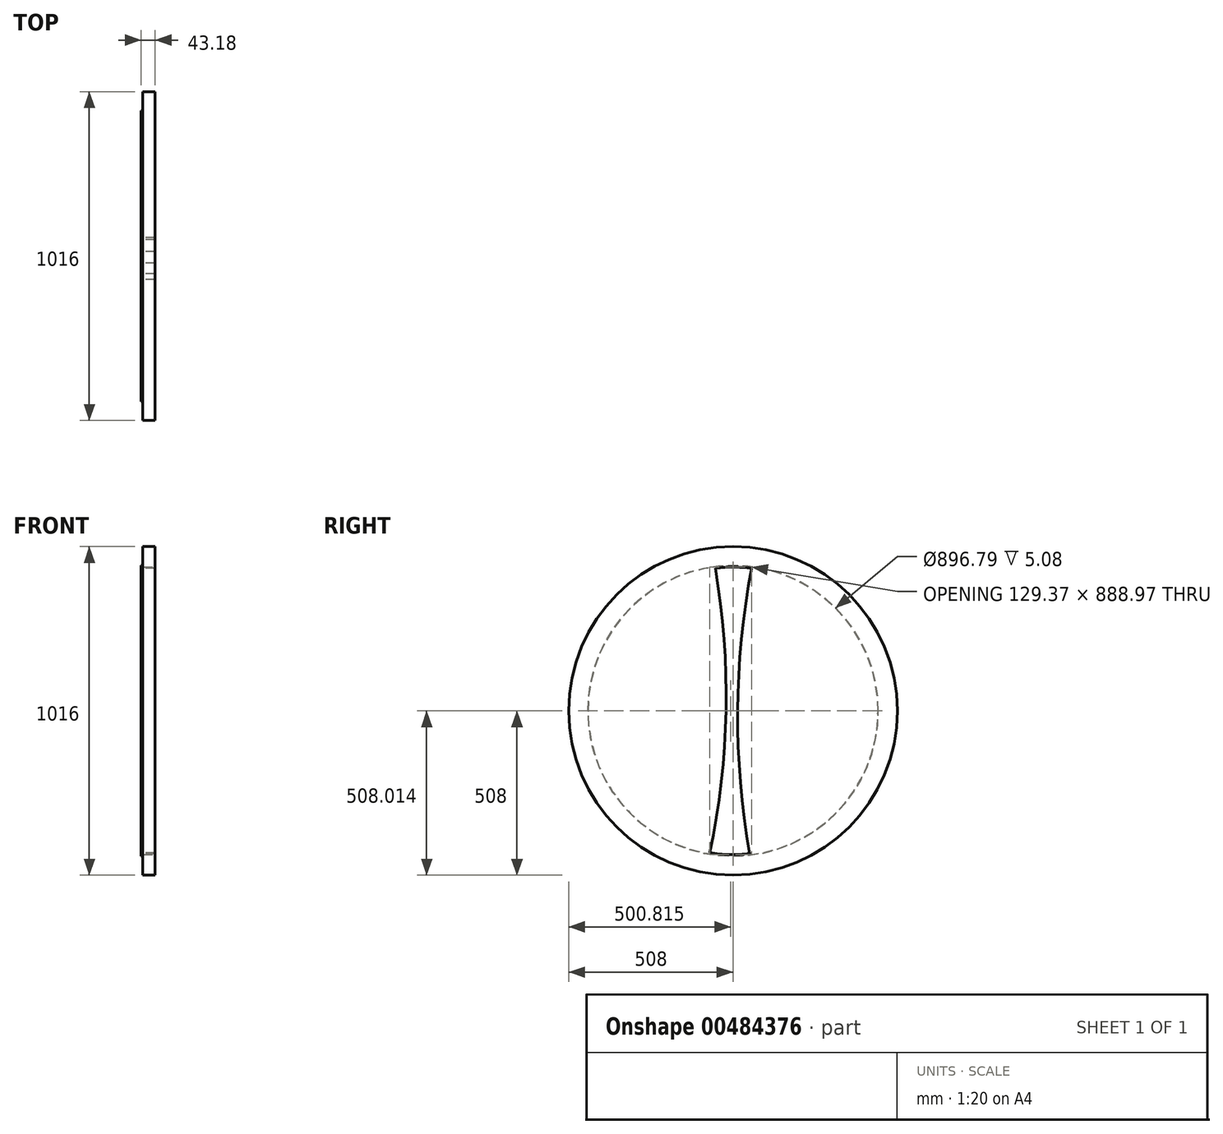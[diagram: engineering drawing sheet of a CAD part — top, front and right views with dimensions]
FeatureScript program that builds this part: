
annotation { "Feature Type Name" : "Feature", "Feature Type Description" : "" }
export const myFeature = defineFeature(function(context is Context, id is Id, definition is map)
    precondition{}
    {
        {
            var Q0;
            Q0=qCreatedBy(makeId("Right.planeOp"),FACE);
            var sketch = newSketch(context, id + "F0", { "sketchPlane" : qUnion([Q0])});
            skCircle(sketch, "E0", {"center": v(0, 0) * mm, "radius": 508 * mm});
            skSolve(sketch);
        }
        {
            var Q0;
            Q0=makeQuery(id+"F0.imprint","IMPRINT",FACE,{"disambiguationData":[TD([[makeQuery(id+"F0.imprint","IMPRINT",EDGE,{"derivedFrom":sQuery(id+"F0.wireOp",EDGE,"E0")}),1.0]])]});
            extrude(context, id + "F1", {"entities" : qUnion([Q0]), "depth" : 38.1 * mm});
        }
        {
            var Q0;
            Q0=makeQuery(id+"F1.opExtrude","CAP_FACE",FACE,{"disambiguationData":[OSD([sQuery(id+"F0.wireOp",EDGE,"E0")])],"isStart":false});
            var sketch = newSketch(context, id + "F2", { "sketchPlane" : qUnion([Q0])});
            skLineSegment(sketch, "E1", {"start": v(-508, 0) * mm, "end": v(508, 0) * mm});
            skSolve(sketch);
        }
        {
            var Q0;
            {var subQ0=sQuery(id+"F2.wireOp",EDGE,"E1");Q0=makeQuery(id+"F2.imprint","IMPRINT",FACE,{"disambiguationData":[TD([[makeQuery(id+"F2.imprint","IMPRINT",EDGE,{"derivedFrom":subQ0}),1.0]])]});}
            var sketch = newSketch(context, id + "F3", { "sketchPlane" : qUnion([Q0])});
            skPoint(sketch, "E2", {"position": v(0, 0) * mm});
            skSolve(sketch);
        }
        {
            var Q0;
            Q0=sQuery(id+"F3.wireOp",VERTEX,"E2");
            var Q1;
            Q1=makeQuery(id+"F1.opExtrude","SWEPT_BODY",BODY,{"disambiguationData":[OSD([sQuery(id+"F0.wireOp",EDGE,"E0")])]});
            hole(context, id + "F4", {"style" : HoleStyle.SIMPLE, "endStyle" : HoleEndStyle.THROUGH, "holeDiameter" : 889 * mm, "isTappedThrough" : true, "tappedDepth" : 12.7 * mm, "tapClearance" : 3, "locations" : qUnion([Q0]), "scope" : qUnion([Q1])});
        }
        {
            var Q0;
            Q0=makeQuery(id+"F1.opExtrude","CAP_FACE",FACE,{"disambiguationData":[OSD([sQuery(id+"F0.wireOp",EDGE,"E0")])],"isStart":true});
            var sketch = newSketch(context, id + "F5", { "sketchPlane" : qUnion([Q0])});
            skLineSegment(sketch, "E3", {"start": v(0, 444.5) * mm, "end": v(0, -444.5) * mm});
            skArc(sketch, "E4", {"start": v(-51.32, -441.53) * mm, "mid": v(-14.44, -0.1) * mm, "end": v(-57.5, 440.77) * mm});
            skArc(sketch, "E5", {"start": v(54.9, 441.1) * mm, "mid": v(21.55, 0.42) * mm, "end": v(71.87, -438.65) * mm});
            skSolve(sketch);
        }
        {
            var Q0;
            Q0 = qSketchRegion(id + "F5", true);
            var Q1;
            {var subQ0=sQuery(id+"F5.wireOp",EDGE,"E3");var subQ3=sQuery(id+"F5.wireOp",EDGE,"q3zEqORE-pkgJ-rEnr-FRpH-zGvHFIiglx1X");var subQ4=makeQuery(id+"F5.imprint","INTERSECT",VERTEX,{"derivedFrom":[subQ0,subQ3]});Q1=makeQuery(id+"F5.imprint","IMPRINT",FACE,{"disambiguationData":[TD([[makeQuery(id+"F5.imprint","IMPRINT",EDGE,{"disambiguationData":[TD([[subQ4,-1.0]])],"derivedFrom":subQ3}),1.0]])]});}
            var Q2;
            {var subQ0=sQuery(id+"F5.wireOp",EDGE,"E3");var subQ3=sQuery(id+"F5.wireOp",EDGE,"q3zEqORE-pkgJ-rEnr-FRpH-zGvHFIiglx1X");var subQ4=makeQuery(id+"F5.imprint","INTERSECT",VERTEX,{"derivedFrom":[subQ0,subQ3]});Q2=makeQuery(id+"F5.imprint","IMPRINT",FACE,{"disambiguationData":[TD([[makeQuery(id+"F5.imprint","IMPRINT",EDGE,{"disambiguationData":[TD([[subQ4,1.0]])],"derivedFrom":subQ3}),1.0]])]});}
            var Q3;
            {var subQ0=sQuery(id+"F5.wireOp",EDGE,"O9KcMm5O-TFmN-3ZNM-UmmH-q29h341Hwobi");var subQ3=sQuery(id+"F5.wireOp",EDGE,"E4");var subQ4=makeQuery(id+"F5.imprint","INTERSECT",VERTEX,{"derivedFrom":[subQ0,subQ3]});Q3=makeQuery(id+"F5.imprint","IMPRINT",FACE,{"disambiguationData":[TD([[makeQuery(id+"F5.imprint","IMPRINT",EDGE,{"disambiguationData":[TD([[subQ4,-1.0]])],"derivedFrom":subQ3}),1.0]])]});}
            var Q4;
            {var subQ0=sQuery(id+"F5.wireOp",EDGE,"O9KcMm5O-TFmN-3ZNM-UmmH-q29h341Hwobi");var subQ3=sQuery(id+"F5.wireOp",EDGE,"E4");var subQ4=makeQuery(id+"F5.imprint","INTERSECT",VERTEX,{"derivedFrom":[subQ0,subQ3]});Q4=makeQuery(id+"F5.imprint","IMPRINT",FACE,{"disambiguationData":[TD([[makeQuery(id+"F5.imprint","IMPRINT",EDGE,{"disambiguationData":[TD([[subQ4,1.0]])],"derivedFrom":subQ3}),1.0]])]});}
            var Q5;
            {var subQ0=sQuery(id+"F5.wireOp",EDGE,"O9KcMm5O-TFmN-3ZNM-UmmH-q29h341Hwobi");var subQ3=sQuery(id+"F5.wireOp",EDGE,"E5");var subQ4=makeQuery(id+"F5.imprint","INTERSECT",VERTEX,{"derivedFrom":[subQ0,subQ3]});Q5=makeQuery(id+"F5.imprint","IMPRINT",FACE,{"disambiguationData":[TD([[makeQuery(id+"F5.imprint","IMPRINT",EDGE,{"disambiguationData":[TD([[subQ4,1.0]])],"derivedFrom":subQ3}),1.0]])]});}
            var Q6;
            {var subQ0=sQuery(id+"F5.wireOp",EDGE,"O9KcMm5O-TFmN-3ZNM-UmmH-q29h341Hwobi");var subQ3=sQuery(id+"F5.wireOp",EDGE,"E5");var subQ4=makeQuery(id+"F5.imprint","INTERSECT",VERTEX,{"derivedFrom":[subQ0,subQ3]});Q6=makeQuery(id+"F5.imprint","IMPRINT",FACE,{"disambiguationData":[TD([[makeQuery(id+"F5.imprint","IMPRINT",EDGE,{"disambiguationData":[TD([[subQ4,-1.0]])],"derivedFrom":subQ3}),1.0]])]});}
            var Q7;
            {var subQ0=sQuery(id+"F5.wireOp",EDGE,"E3");var subQ3=sQuery(id+"F5.wireOp",EDGE,"ECyhuEZf-V5Dx-fmmA-phiA-keAbpECHN96i");var subQ4=makeQuery(id+"F5.imprint","INTERSECT",VERTEX,{"derivedFrom":[subQ0,subQ3]});Q7=makeQuery(id+"F5.imprint","IMPRINT",FACE,{"disambiguationData":[TD([[makeQuery(id+"F5.imprint","IMPRINT",EDGE,{"disambiguationData":[TD([[subQ4,-1.0]])],"derivedFrom":subQ3}),1.0]])]});}
            var Q8;
            {var subQ0=sQuery(id+"F5.wireOp",EDGE,"E3");var subQ3=sQuery(id+"F5.wireOp",EDGE,"ECyhuEZf-V5Dx-fmmA-phiA-keAbpECHN96i");var subQ4=makeQuery(id+"F5.imprint","INTERSECT",VERTEX,{"derivedFrom":[subQ0,subQ3]});Q8=makeQuery(id+"F5.imprint","IMPRINT",FACE,{"disambiguationData":[TD([[makeQuery(id+"F5.imprint","IMPRINT",EDGE,{"disambiguationData":[TD([[subQ4,1.0]])],"derivedFrom":subQ3}),1.0]])]});}
            extrude(context, id + "F6", {"entities" : qUnion([Q0, Q1, Q2, Q3, Q4, Q5, Q6, Q7, Q8]), "operationType" : NewBodyOperationType.ADD, "depth" : -38.1 * mm});
        }
        {
            var Q0;
            {var subQ0=sQuery(id+"F0.wireOp",EDGE,"E0");Q0=makeQuery(id+"F6.boolean.opBoolean","MERGE",FACE,{"derivedFrom":[makeQuery(id+"F1.opExtrude","CAP_FACE",FACE,{"disambiguationData":[OSD([subQ0])],"isStart":true}),makeQuery(id+"F6.opExtrude","CAP_FACE",FACE,{"disambiguationData":[OSD([subQ0,sQuery(id+"F4.hole-0.sketch.wireOp",EDGE,"core_line_2"),sQuery(id+"F5.wireOp",EDGE,"q3zEqORE-pkgJ-rEnr-FRpH-zGvHFIiglx1X"),sQuery(id+"F5.wireOp",EDGE,"ECyhuEZf-V5Dx-fmmA-phiA-keAbpECHN96i"),sQuery(id+"F5.wireOp",EDGE,"E4"),sQuery(id+"F5.wireOp",EDGE,"E5")])],"isStart":true})]});}
            var sketch = newSketch(context, id + "F7", { "sketchPlane" : qUnion([Q0])});
            skCircle(sketch, "E6", {"center": v(0, 0) * mm, "radius": 448.4 * mm});
            skCircle(sketch, "E7", {"center": v(0, 0) * mm, "radius": 449.21 * mm});
            skSolve(sketch);
        }
        {
            var Q0;
            Q0=makeQuery(id+"F7.imprint","IMPRINT",FACE,{"disambiguationData":[TD([[makeQuery(id+"F7.imprint","IMPRINT",EDGE,{"derivedFrom":sQuery(id+"F7.wireOp",EDGE,"E6")}),-1.0]])]});
            extrude(context, id + "F8", {"entities" : qUnion([Q0]), "operationType" : NewBodyOperationType.ADD, "depth" : 5.08 * mm});
        }
    });
